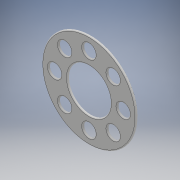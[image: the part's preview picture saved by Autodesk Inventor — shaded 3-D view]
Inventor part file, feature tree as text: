
AUTODESK INVENTOR PART (.ipt)
format: ipt  version: 2018 (Build 220112000, 112)  size: 396,288 bytes
history: native  units: mm
features: extrude x1, fillet x1, sketch x1
ambient origin geometry x8: Origin, YZ Plane, XZ Plane, XY Plane, X Axis, Y Axis, Z Axis, Center Point
bodies: Solid1 (feature_tree)
feature tree (3):
  extrude  "Extrusion1"  Depth=0.25mm
  fillet  "Fillet1"  [1 undecoded]
  sketch  "Sketch1"  dims[d0=0.5mm d1=0.0mm d2=0.25mm]
note: 1 required parameter value undecoded (feature->parameter linkage not recoverable at this tier; creation-order binding heuristic only, values carry confidence <= 0.55)
